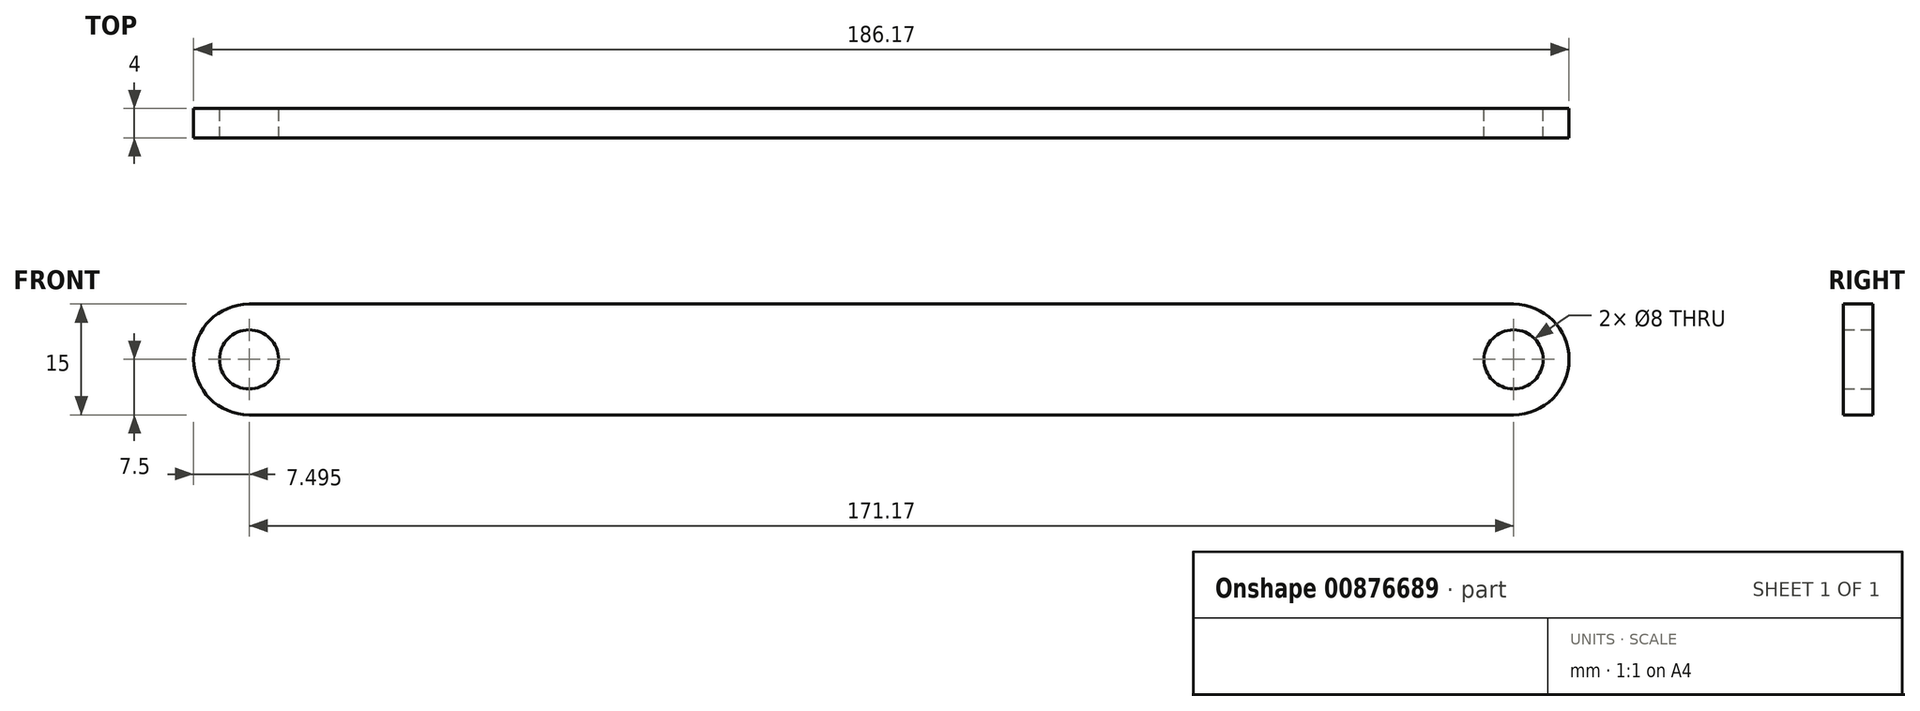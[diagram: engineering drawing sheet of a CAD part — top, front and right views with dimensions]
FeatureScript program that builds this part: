
annotation { "Feature Type Name" : "Feature", "Feature Type Description" : "" }
export const myFeature = defineFeature(function(context is Context, id is Id, definition is map)
    precondition{}
    {
        {
            var Q0;
            Q0=qCreatedBy(makeId("Front.planeOp"),FACE);
            var sketch = newSketch(context, id + "F0", { "sketchPlane" : qUnion([Q0])});
            skCircle(sketch, "E0", {"center": v(85.48, 0) * mm, "radius": 4 * mm});
            skCircle(sketch, "E1", {"center": v(-85.7, 0) * mm, "radius": 4 * mm});
            skArc(sketch, "E2", {"start": v(-85.7, 7.5) * mm, "mid": v(-93.2, 0) * mm, "end": v(-85.7, -7.5) * mm});
            skArc(sketch, "E3", {"start": v(85.48, -7.5) * mm, "mid": v(92.98, 0) * mm, "end": v(85.48, 7.5) * mm});
            skLineSegment(sketch, "E4", {"start": v(-85.7, 7.5) * mm, "end": v(85.48, 7.5) * mm});
            skLineSegment(sketch, "E5", {"start": v(-85.7, -7.5) * mm, "end": v(85.48, -7.5) * mm});
            skSolve(sketch);
        }
        {
            var Q0;
            Q0=makeQuery(id+"F0.imprint","IMPRINT",FACE,{"disambiguationData":[TD([[makeQuery(id+"F0.imprint","IMPRINT",EDGE,{"derivedFrom":sQuery(id+"F0.wireOp",EDGE,"E0")}),-1.0]])]});
            extrude(context, id + "F1", {"entities" : qUnion([Q0]), "depth" : 4 * mm, "offsetDistance" : 25 * mm});
        }
    });
